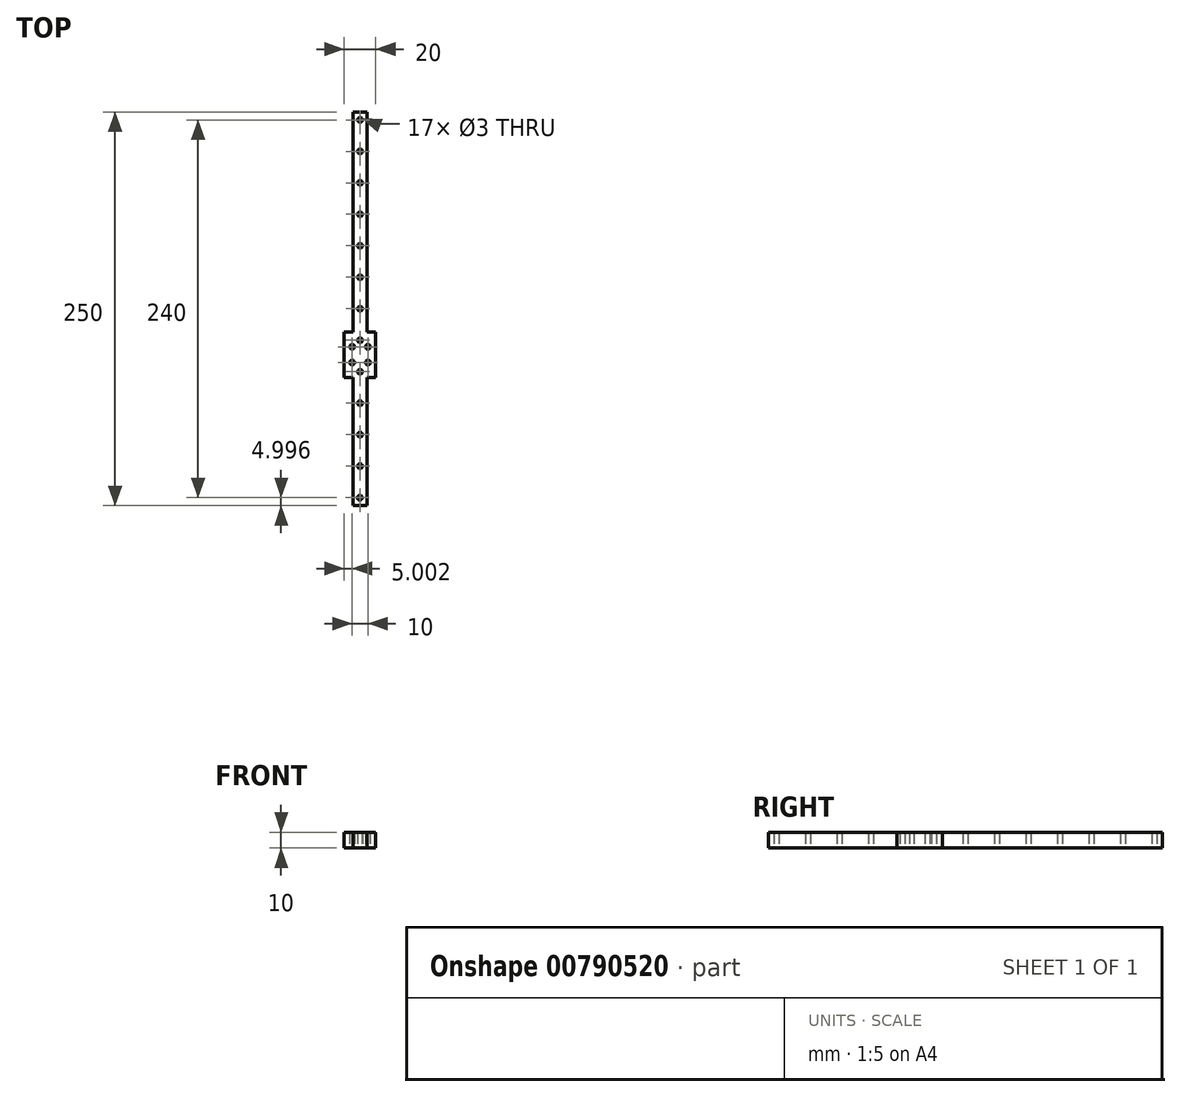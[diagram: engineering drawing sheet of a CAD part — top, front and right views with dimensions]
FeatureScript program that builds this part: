
annotation { "Feature Type Name" : "Feature", "Feature Type Description" : "" }
export const myFeature = defineFeature(function(context is Context, id is Id, definition is map)
    precondition{}
    {
        {
            var Q0;
            Q0=qCreatedBy(makeId("Top.planeOp"),FACE);
            var sketch = newSketch(context, id + "F0", { "sketchPlane" : qUnion([Q0])});
            skLineSegment(sketch, "E0.bottom", {"start": v(-255.73, 143.83) * mm, "end": v(-246.73, 143.83) * mm});
            skLineSegment(sketch, "E0.top", {"start": v(-255.73, -106.17) * mm, "end": v(-246.73, -106.17) * mm});
            skLineSegment(sketch, "E0.left", {"start": v(-255.73, 143.83) * mm, "end": v(-255.73, -106.17) * mm});
            skLineSegment(sketch, "E0.right", {"start": v(-246.73, 143.83) * mm, "end": v(-246.73, -106.17) * mm});
            skCircle(sketch, "E1", {"center": v(-251.23, 138.83) * mm, "radius": 1.5 * mm});
            skPoint(sketch, "E1.centerSnap0", {"position": v(-251.23, 143.83) * mm});
            skCircle(sketch, "E2", {"center": v(-251.23, 118.83) * mm, "radius": 1.5 * mm});
            skCircle(sketch, "E3", {"center": v(-251.23, 98.83) * mm, "radius": 1.5 * mm});
            skCircle(sketch, "E4", {"center": v(-251.23, 78.83) * mm, "radius": 1.5 * mm});
            skCircle(sketch, "E5", {"center": v(-251.23, 58.83) * mm, "radius": 1.5 * mm});
            skCircle(sketch, "E6", {"center": v(-251.23, 38.83) * mm, "radius": 1.5 * mm});
            skCircle(sketch, "E7", {"center": v(-251.23, 18.83) * mm, "radius": 1.5 * mm});
            skCircle(sketch, "E8", {"center": v(-251.23, -1.17) * mm, "radius": 1.5 * mm});
            skCircle(sketch, "E9", {"center": v(-251.23, -21.17) * mm, "radius": 1.5 * mm});
            skCircle(sketch, "E10", {"center": v(-251.23, -41.17) * mm, "radius": 1.5 * mm});
            skCircle(sketch, "E11", {"center": v(-251.23, -61.17) * mm, "radius": 1.5 * mm});
            skCircle(sketch, "E12", {"center": v(-251.23, -81.17) * mm, "radius": 1.5 * mm});
            skCircle(sketch, "E13", {"center": v(-251.33, -101.17) * mm, "radius": 1.5 * mm});
            skLineSegment(sketch, "E14.bottom", {"start": v(-241.23, 4.13) * mm, "end": v(-241.23, -24.77) * mm});
            skLineSegment(sketch, "E14.top", {"start": v(-261.23, 4.13) * mm, "end": v(-261.23, -24.77) * mm});
            skLineSegment(sketch, "E14.left", {"start": v(-241.23, 4.13) * mm, "end": v(-261.23, 4.13) * mm});
            skLineSegment(sketch, "E14.right", {"start": v(-241.23, -24.77) * mm, "end": v(-261.23, -24.77) * mm});
            skCircle(sketch, "E15", {"center": v(-256.23, -5.32) * mm, "radius": 1.5 * mm});
            skCircle(sketch, "E16", {"center": v(-246.23, -5.32) * mm, "radius": 1.5 * mm});
            skCircle(sketch, "E17", {"center": v(-246.23, -15.32) * mm, "radius": 1.5 * mm});
            skCircle(sketch, "E18", {"center": v(-256.23, -15.32) * mm, "radius": 1.5 * mm});
            skSolve(sketch);
        }
        {
            var Q0;
            Q0 = qSketchRegion(id + "F0", true);
            extrude(context, id + "F1", {"entities" : qUnion([Q0]), "depth" : 10 * mm, "offsetDistance" : 25 * mm});
        }
    });
